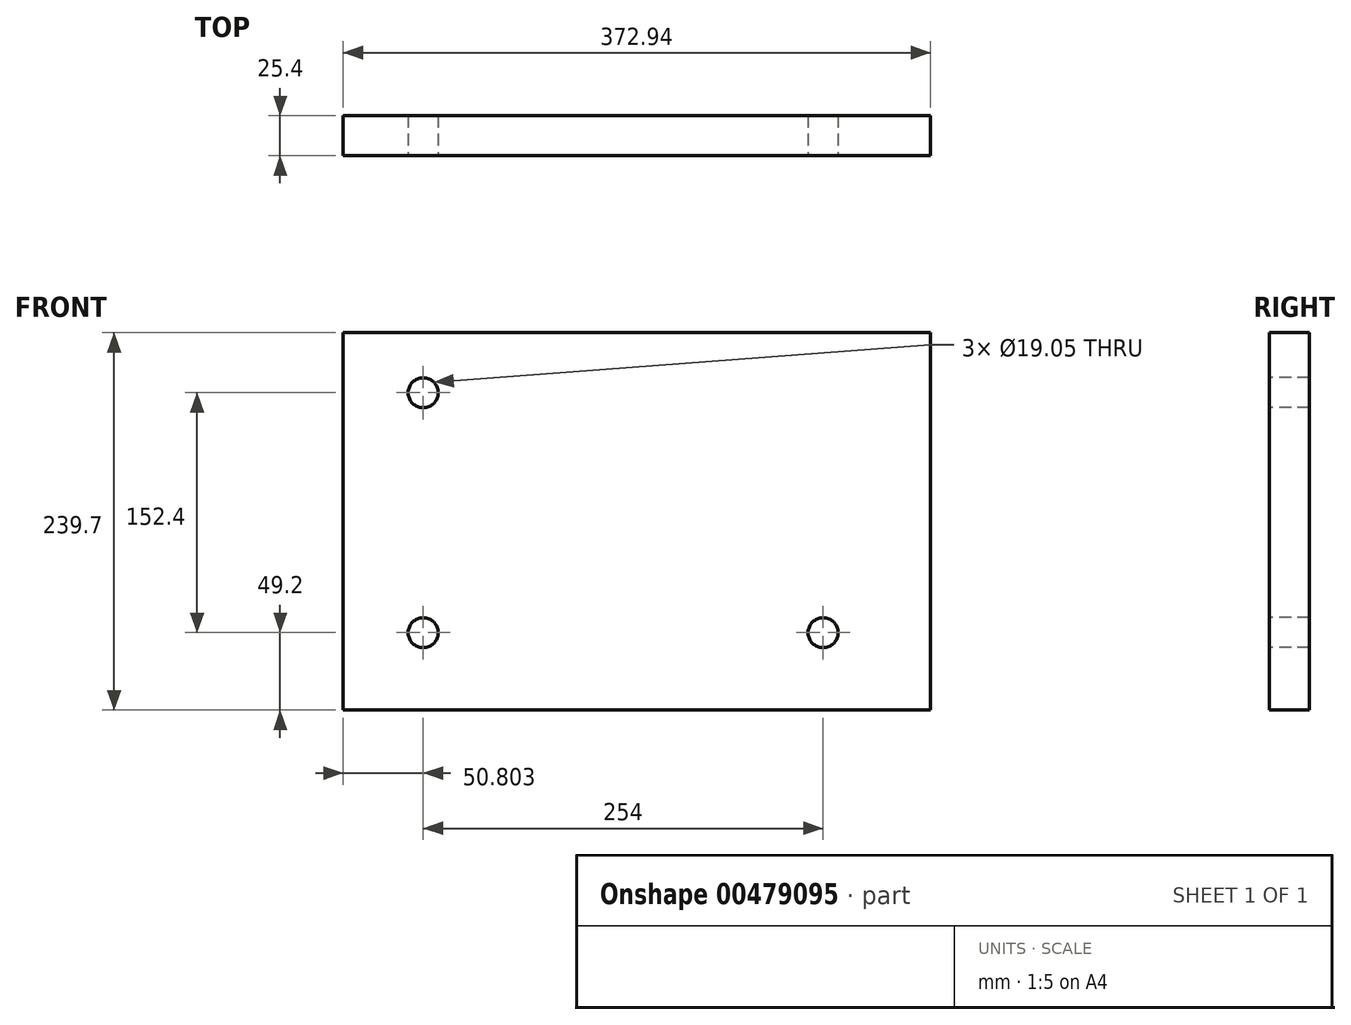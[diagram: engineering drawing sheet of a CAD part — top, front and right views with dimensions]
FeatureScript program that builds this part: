
annotation { "Feature Type Name" : "Feature", "Feature Type Description" : "" }
export const myFeature = defineFeature(function(context is Context, id is Id, definition is map)
    precondition{}
    {
        {
            var Q0;
            Q0=qCreatedBy(makeId("Front.planeOp"),FACE);
            var sketch = newSketch(context, id + "F0", { "sketchPlane" : qUnion([Q0])});
            skLineSegment(sketch, "E0.bottom", {"start": v(186.47, -119.85) * mm, "end": v(-186.47, -119.85) * mm});
            skLineSegment(sketch, "E0.top", {"start": v(186.47, 119.85) * mm, "end": v(-186.47, 119.85) * mm});
            skLineSegment(sketch, "E0.left", {"start": v(186.47, -119.85) * mm, "end": v(186.47, 119.85) * mm});
            skLineSegment(sketch, "E0.right", {"start": v(-186.47, -119.85) * mm, "end": v(-186.47, 119.85) * mm});
            skPoint(sketch, "E0.middle", {"position": v(0, 0) * mm});
            skSolve(sketch);
        }
        {
            var Q0;
            Q0 = qSketchRegion(id + "F0", true);
            extrude(context, id + "F1", {"entities" : qUnion([Q0]), "depth" : 25.4 * mm});
        }
        {
            var Q0;
            Q0=makeQuery(id+"F1.opExtrude","CAP_FACE",FACE,{"disambiguationData":[OSD([sQuery(id+"F0.wireOp",EDGE,"E0.bottom"),sQuery(id+"F0.wireOp",EDGE,"E0.top"),sQuery(id+"F0.wireOp",EDGE,"E0.left"),sQuery(id+"F0.wireOp",EDGE,"E0.right")])],"isStart":false});
            var sketch = newSketch(context, id + "F2", { "sketchPlane" : qUnion([Q0])});
            skLineSegment(sketch, "E1.bottom", {"start": v(-135.67, 81.75) * mm, "end": v(118.33, 81.75) * mm, "construction": true});
            skLineSegment(sketch, "E1.top", {"start": v(-135.67, -70.65) * mm, "end": v(118.33, -70.65) * mm, "construction": true});
            skLineSegment(sketch, "E1.left", {"start": v(-135.67, 81.75) * mm, "end": v(-135.67, -70.65) * mm, "construction": true});
            skLineSegment(sketch, "E1.right", {"start": v(118.33, 81.75) * mm, "end": v(118.33, -70.65) * mm, "construction": true});
            skSolve(sketch);
        }
        {
            var Q0;
            Q0=sQuery(id+"F2.wireOp",VERTEX,"E1.left.start");
            var Q1;
            Q1=sQuery(id+"F2.wireOp",VERTEX,"E1.left.end");
            var Q2;
            Q2=sQuery(id+"F2.wireOp",VERTEX,"E1.top.end");
            var Q3;
            Q3=makeQuery(id+"F1.opExtrude","SWEPT_BODY",BODY,{"disambiguationData":[OSD([sQuery(id+"F0.wireOp",EDGE,"E0.bottom"),sQuery(id+"F0.wireOp",EDGE,"E0.top"),sQuery(id+"F0.wireOp",EDGE,"E0.left"),sQuery(id+"F0.wireOp",EDGE,"E0.right")])]});
            hole(context, id + "F3", {"style" : HoleStyle.SIMPLE, "endStyle" : HoleEndStyle.THROUGH, "holeDiameter" : 19.05 * mm, "isTappedThrough" : true, "tappedDepth" : 12.7 * mm, "tapClearance" : 3, "locations" : qUnion([Q0, Q1, Q2]), "scope" : qUnion([Q3])});
        }
    });
